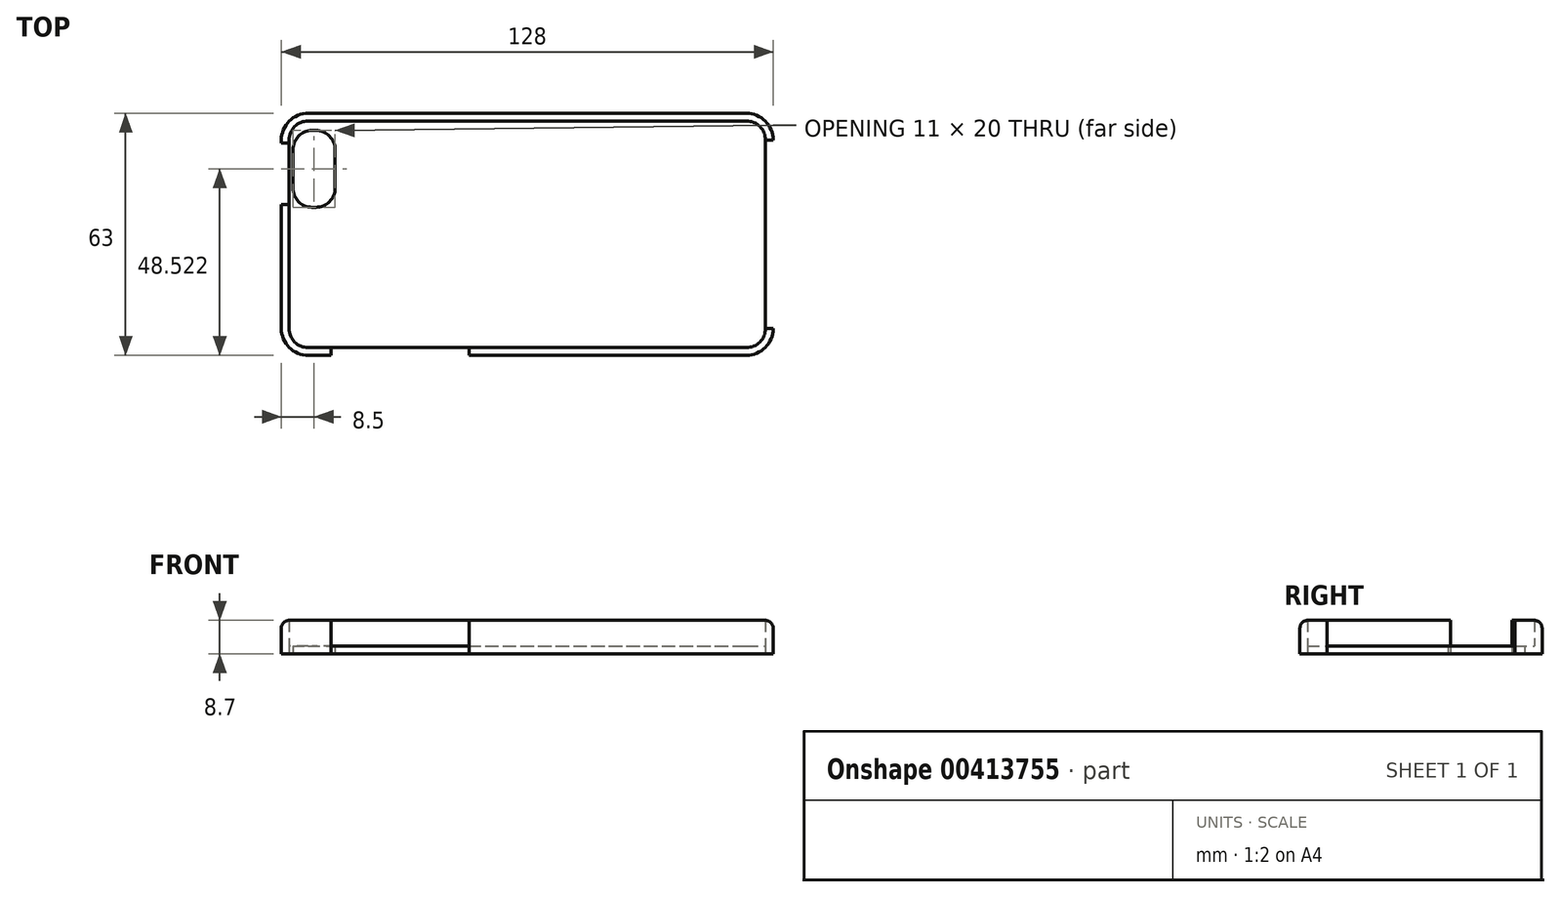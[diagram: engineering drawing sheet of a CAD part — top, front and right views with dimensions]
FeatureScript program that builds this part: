
annotation { "Feature Type Name" : "Feature", "Feature Type Description" : "" }
export const myFeature = defineFeature(function(context is Context, id is Id, definition is map)
    precondition{}
    {
        {
            var Q0;
            Q0=qCreatedBy(makeId("Top.planeOp"),FACE);
            var sketch = newSketch(context, id + "F0", { "sketchPlane" : qUnion([Q0])});
            skLineSegment(sketch, "E0.bottom", {"start": v(-57, 29.5) * mm, "end": v(57, 29.5) * mm});
            skLineSegment(sketch, "E0.top", {"start": v(-57, -29.5) * mm, "end": v(57, -29.5) * mm});
            skLineSegment(sketch, "E0.left", {"start": v(-62, 24.5) * mm, "end": v(-62, -24.5) * mm});
            skLineSegment(sketch, "E0.right", {"start": v(62, 24.5) * mm, "end": v(62, -24.5) * mm});
            skPoint(sketch, "E0.middle", {"position": v(0, 0) * mm});
            skPoint(sketch, "E1.visualSharp", {"position": v(62, 29.5) * mm});
            skArc(sketch, "E1.filletArc", {"start": v(62, 24.5) * mm, "mid": v(60.54, 28.04) * mm, "end": v(57, 29.5) * mm});
            skPoint(sketch, "E2.visualSharp", {"position": v(62, -29.5) * mm});
            skArc(sketch, "E2.filletArc", {"start": v(57, -29.5) * mm, "mid": v(60.54, -28.04) * mm, "end": v(62, -24.5) * mm});
            skPoint(sketch, "E3.visualSharp", {"position": v(-62, -29.5) * mm});
            skArc(sketch, "E3.filletArc", {"start": v(-62, -24.5) * mm, "mid": v(-60.54, -28.04) * mm, "end": v(-57, -29.5) * mm});
            skPoint(sketch, "E4.visualSharp", {"position": v(-62, 29.5) * mm});
            skArc(sketch, "E4.filletArc", {"start": v(-57, 29.5) * mm, "mid": v(-60.54, 28.04) * mm, "end": v(-62, 24.5) * mm});
            skLineSegment(sketch, "E5.bottom", {"start": v(-55, 27.02) * mm, "end": v(-56, 27.02) * mm});
            skLineSegment(sketch, "E5.top", {"start": v(-55, 7.02) * mm, "end": v(-56, 7.02) * mm});
            skLineSegment(sketch, "E5.left", {"start": v(-50, 22.02) * mm, "end": v(-50, 12.02) * mm});
            skLineSegment(sketch, "E5.right", {"start": v(-61, 22.02) * mm, "end": v(-61, 12.02) * mm});
            skPoint(sketch, "E6.visualSharp", {"position": v(-61, 27.02) * mm});
            skArc(sketch, "E6.filletArc", {"start": v(-56, 27.02) * mm, "mid": v(-59.54, 25.56) * mm, "end": v(-61, 22.02) * mm});
            skPoint(sketch, "E7.visualSharp", {"position": v(-50, 27.02) * mm});
            skArc(sketch, "E7.filletArc", {"start": v(-50, 22.02) * mm, "mid": v(-51.46, 25.56) * mm, "end": v(-55, 27.02) * mm});
            skPoint(sketch, "E8.visualSharp", {"position": v(-50, 7.02) * mm});
            skArc(sketch, "E8.filletArc", {"start": v(-55, 7.02) * mm, "mid": v(-51.46, 8.49) * mm, "end": v(-50, 12.02) * mm});
            skPoint(sketch, "E9.visualSharp", {"position": v(-61, 7.02) * mm});
            skArc(sketch, "E9.filletArc", {"start": v(-61, 12.02) * mm, "mid": v(-59.54, 8.49) * mm, "end": v(-56, 7.02) * mm});
            skLineSegment(sketch, "E10.0", {"start": v(-57, 31.5) * mm, "end": v(57, 31.5) * mm});
            skArc(sketch, "E11.0", {"start": v(64, 24.5) * mm, "mid": v(61.95, 29.45) * mm, "end": v(57, 31.5) * mm});
            skLineSegment(sketch, "E11.1", {"start": v(64, 24.5) * mm, "end": v(64, -24.5) * mm});
            skArc(sketch, "E11.2", {"start": v(57, -31.5) * mm, "mid": v(61.95, -29.45) * mm, "end": v(64, -24.5) * mm});
            skArc(sketch, "E11.3", {"start": v(-57, 31.5) * mm, "mid": v(-61.95, 29.45) * mm, "end": v(-64, 24.5) * mm});
            skLineSegment(sketch, "E11.4", {"start": v(-64, 24.5) * mm, "end": v(-64, -24.5) * mm});
            skArc(sketch, "E11.5", {"start": v(-64, -24.5) * mm, "mid": v(-61.95, -29.45) * mm, "end": v(-57, -31.5) * mm});
            skLineSegment(sketch, "E11.6", {"start": v(-57, -31.5) * mm, "end": v(57, -31.5) * mm});
            skSolve(sketch);
        }
        {
            var Q0;
            Q0=makeQuery(id+"F0.imprint","IMPRINT",FACE,{"disambiguationData":[TD([[makeQuery(id+"F0.imprint","IMPRINT",EDGE,{"derivedFrom":sQuery(id+"F0.wireOp",EDGE,"E0.bottom")}),-1.0]])]});
            extrude(context, id + "F1", {"entities" : qUnion([Q0]), "depth" : 2 * mm});
        }
        {
            var Q0;
            Q0 = qSketchRegion(id + "F0", true);
            extrude(context, id + "F2", {"entities" : qUnion([Q0]), "operationType" : NewBodyOperationType.ADD, "depth" : 8.7 * mm});
        }
        {
            var Q0;
            Q0=makeQuery(id+"F2.opExtrude","SWEPT_FACE",FACE,{"disambiguationData":[OSD([sQuery(id+"F0.wireOp",EDGE,"E11.6")])]});
            var sketch = newSketch(context, id + "F3", { "sketchPlane" : qUnion([Q0])});
            skLineSegment(sketch, "E12.bottom", {"start": v(-51.08, 8.7) * mm, "end": v(-15.08, 8.7) * mm});
            skLineSegment(sketch, "E12.top", {"start": v(-51.08, 0) * mm, "end": v(-15.08, 0) * mm});
            skLineSegment(sketch, "E12.left", {"start": v(-51.08, 8.7) * mm, "end": v(-51.08, 0) * mm});
            skLineSegment(sketch, "E12.right", {"start": v(-15.08, 8.7) * mm, "end": v(-15.08, 0) * mm});
            skSolve(sketch);
        }
        {
            var Q0;
            Q0=makeQuery(id+"F3.imprint","IMPRINT",FACE,{"disambiguationData":[TD([[makeQuery(id+"F3.imprint","IMPRINT",EDGE,{"derivedFrom":sQuery(id+"F3.wireOp",EDGE,"E12.bottom")}),-1.0]])]});
            extrude(context, id + "F4", {"entities" : qUnion([Q0]), "operationType" : NewBodyOperationType.REMOVE, "oppositeDirection" : true, "depth" : 2 * mm});
        }
        {
            var Q0;
            Q0=makeQuery(id+"F2.opExtrude","SWEPT_FACE",FACE,{"disambiguationData":[OSD([sQuery(id+"F0.wireOp",EDGE,"E11.1")])]});
            extrude(context, id + "F5", {"entities" : qUnion([Q0]), "operationType" : NewBodyOperationType.ADD, "oppositeDirection" : true, "depth" : 2 * mm});
        }
        {
            var Q0;
            Q0=makeQuery(id+"F2.opExtrude","SWEPT_FACE",FACE,{"disambiguationData":[OSD([sQuery(id+"F0.wireOp",EDGE,"E11.1")])]});
            extrude(context, id + "F6", {"entities" : qUnion([Q0]), "operationType" : NewBodyOperationType.ADD, "oppositeDirection" : true, "depth" : 2 * mm});
        }
        {
            var Q0;
            Q0=makeQuery(id+"F2.opExtrude","SWEPT_FACE",FACE,{"disambiguationData":[OSD([sQuery(id+"F0.wireOp",EDGE,"E11.1")])]});
            extrude(context, id + "F7", {"entities" : qUnion([Q0]), "operationType" : NewBodyOperationType.REMOVE, "oppositeDirection" : true, "depth" : 2 * mm});
        }
        {
            var Q0;
            Q0=makeQuery(id+"F2.opExtrude","SWEPT_FACE",FACE,{"disambiguationData":[OSD([sQuery(id+"F0.wireOp",EDGE,"E11.4")])]});
            var sketch = newSketch(context, id + "F8", { "sketchPlane" : qUnion([Q0])});
            skLineSegment(sketch, "E13.bottom", {"start": v(-23.72, 8.7) * mm, "end": v(-7.72, 8.7) * mm});
            skLineSegment(sketch, "E13.top", {"start": v(-23.72, 0) * mm, "end": v(-7.72, 0) * mm});
            skLineSegment(sketch, "E13.left", {"start": v(-23.72, 8.7) * mm, "end": v(-23.72, 0) * mm});
            skLineSegment(sketch, "E13.right", {"start": v(-7.72, 8.7) * mm, "end": v(-7.72, 0) * mm});
            skSolve(sketch);
        }
        {
            var Q0;
            Q0=makeQuery(id+"F8.imprint","IMPRINT",FACE,{"disambiguationData":[TD([[makeQuery(id+"F8.imprint","IMPRINT",EDGE,{"derivedFrom":sQuery(id+"F8.wireOp",EDGE,"E13.bottom")}),-1.0]])]});
            extrude(context, id + "F9", {"entities" : qUnion([Q0]), "operationType" : NewBodyOperationType.REMOVE, "oppositeDirection" : true, "depth" : 2 * mm});
        }
        {
            var Q0;
            Q0=makeQuery(id+"F2.opExtrude","CAP_EDGE",EDGE,{"disambiguationData":[OSD([sQuery(id+"F0.wireOp",EDGE,"E11.0")])],"isStart":false});
            var Q1;
            Q1=makeQuery(id+"F2.opExtrude","CAP_EDGE",EDGE,{"disambiguationData":[OSD([sQuery(id+"F0.wireOp",EDGE,"E10.0")])],"isStart":false});
            var Q2;
            Q2=makeQuery(id+"F2.opExtrude","CAP_EDGE",EDGE,{"disambiguationData":[OSD([sQuery(id+"F0.wireOp",EDGE,"E11.3")])],"isStart":false});
            fillet(context, id + "F10", {"entities" : qUnion([Q0, Q1, Q2]), "radius" : 2 * mm, "tangentPropagation" : true, "allowEdgeOverflow" : false});
        }
        {
            var Q0;
            {var subQ0=sQuery(id+"F0.wireOp",EDGE,"E11.5");var subQ1=sQuery(id+"F0.wireOp",EDGE,"E11.4");Q0=makeQuery(id+"F9.boolean.opBoolean","SPLIT",EDGE,{"disambiguationData":[TD([makeQuery(id+"F2.opExtrude","SWEPT_FACE",FACE,{"disambiguationData":[OSD([subQ0])]})])],"derivedFrom":makeQuery(id+"F2.opExtrude","CAP_EDGE",EDGE,{"disambiguationData":[OSD([subQ1])],"isStart":false})});}
            var Q1;
            {var subQ0=sQuery(id+"F0.wireOp",EDGE,"E11.6");var subQ1=sQuery(id+"F0.wireOp",EDGE,"E11.5");Q1=makeQuery(id+"F4.boolean.opBoolean","SPLIT",EDGE,{"disambiguationData":[TD([makeQuery(id+"F2.opExtrude","SWEPT_FACE",FACE,{"disambiguationData":[OSD([subQ1])]})])],"derivedFrom":makeQuery(id+"F2.opExtrude","CAP_EDGE",EDGE,{"disambiguationData":[OSD([subQ0])],"isStart":false})});}
            var Q2;
            Q2=makeQuery(id+"F2.opExtrude","CAP_EDGE",EDGE,{"disambiguationData":[OSD([sQuery(id+"F0.wireOp",EDGE,"E11.5")])],"isStart":false});
            var Q3;
            {var subQ0=sQuery(id+"F0.wireOp",EDGE,"E11.6");var subQ1=sQuery(id+"F0.wireOp",EDGE,"E11.2");Q3=makeQuery(id+"F4.boolean.opBoolean","SPLIT",EDGE,{"disambiguationData":[TD([makeQuery(id+"F2.opExtrude","SWEPT_FACE",FACE,{"disambiguationData":[OSD([subQ1])]})])],"derivedFrom":makeQuery(id+"F2.opExtrude","CAP_EDGE",EDGE,{"disambiguationData":[OSD([subQ0])],"isStart":false})});}
            var Q4;
            Q4=makeQuery(id+"F2.opExtrude","CAP_EDGE",EDGE,{"disambiguationData":[OSD([sQuery(id+"F0.wireOp",EDGE,"E11.2")])],"isStart":false});
            fillet(context, id + "F11", {"entities" : qUnion([Q0, Q1, Q2, Q3, Q4]), "radius" : 2 * mm, "tangentPropagation" : true, "allowEdgeOverflow" : false});
        }
    });
